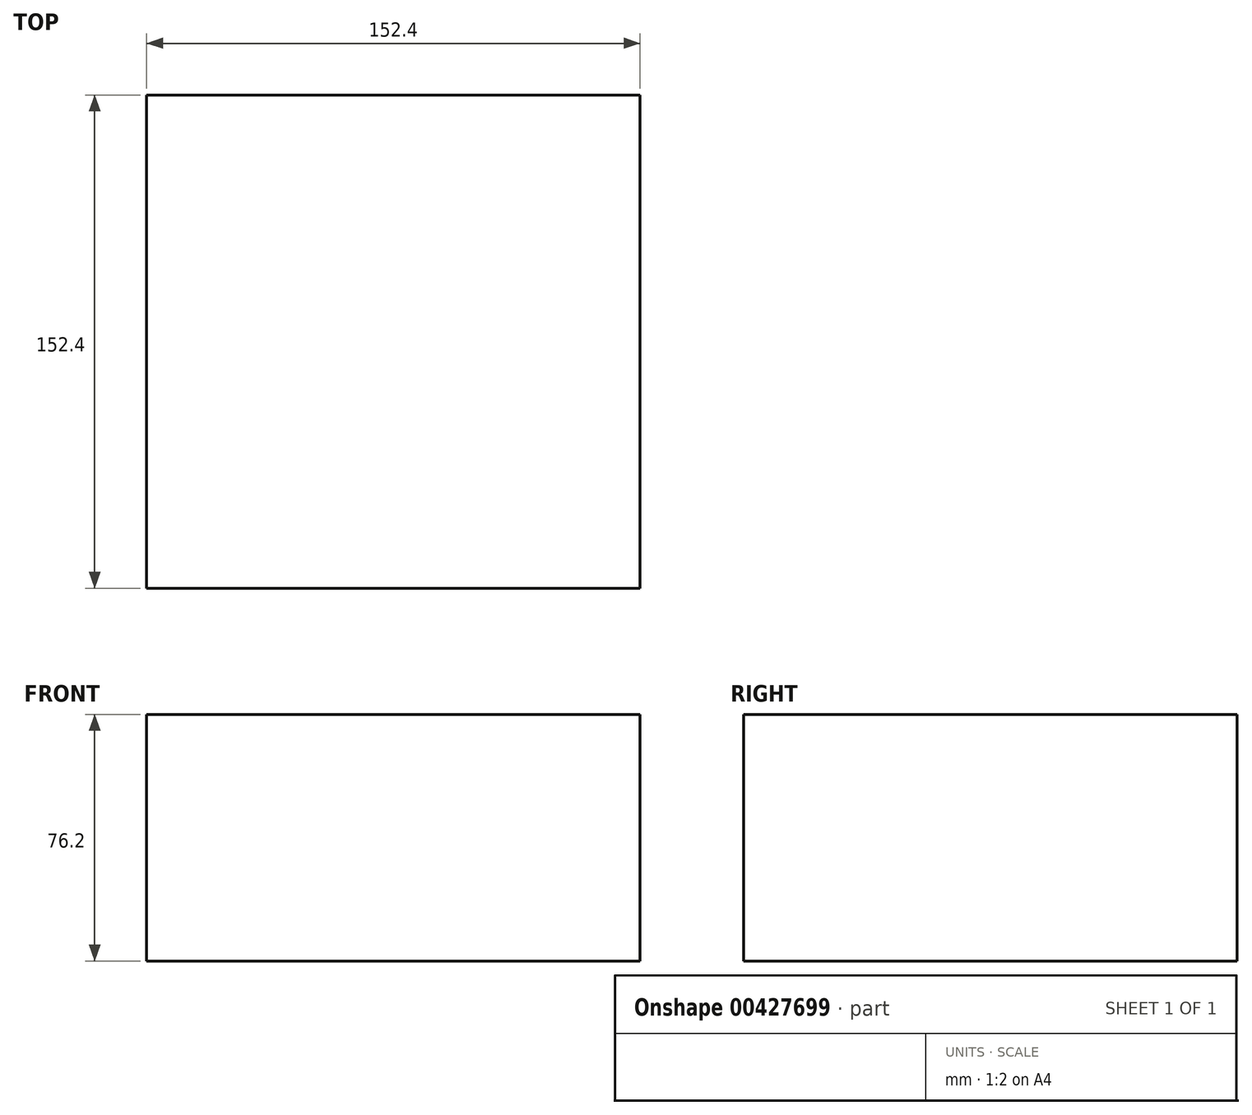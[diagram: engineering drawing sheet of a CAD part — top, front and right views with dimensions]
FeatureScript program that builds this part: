
annotation { "Feature Type Name" : "Feature", "Feature Type Description" : "" }
export const myFeature = defineFeature(function(context is Context, id is Id, definition is map)
    precondition{}
    {
        {
            var Q0;
            Q0=qCreatedBy(makeId("Top.planeOp"),FACE);
            var sketch = newSketch(context, id + "F0", { "sketchPlane" : qUnion([Q0])});
            skLineSegment(sketch, "E0.bottom", {"start": v(0, 0) * mm, "end": v(152.4, 0) * mm});
            skLineSegment(sketch, "E0.top", {"start": v(0, 152.4) * mm, "end": v(152.4, 152.4) * mm});
            skLineSegment(sketch, "E0.left", {"start": v(0, 0) * mm, "end": v(0, 152.4) * mm});
            skLineSegment(sketch, "E0.right", {"start": v(152.4, 0) * mm, "end": v(152.4, 152.4) * mm});
            skSolve(sketch);
        }
        {
            var Q0;
            Q0=makeQuery(id+"F0.imprint","IMPRINT",FACE,{"disambiguationData":[TD([[makeQuery(id+"F0.imprint","IMPRINT",EDGE,{"derivedFrom":sQuery(id+"F0.wireOp",EDGE,"E0.bottom")}),1.0]])]});
            extrude(context, id + "F1", {"entities" : qUnion([Q0]), "depth" : 76.2 * mm, "offsetDistance" : 25.4 * mm});
        }
    });
